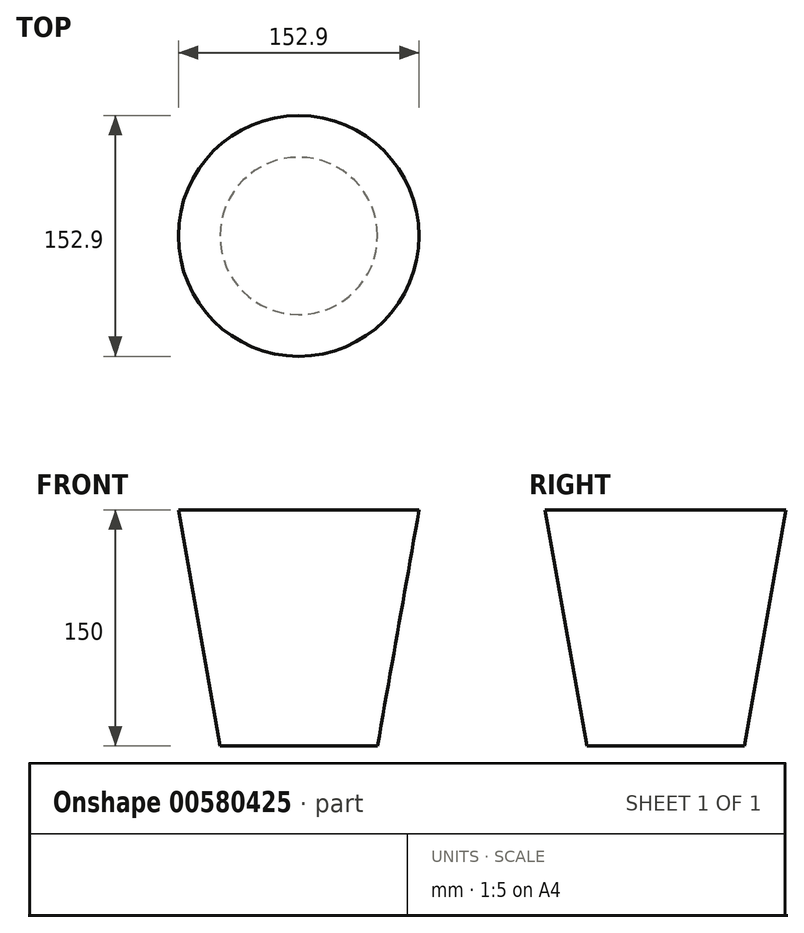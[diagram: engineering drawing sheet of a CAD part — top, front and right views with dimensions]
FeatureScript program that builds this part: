
annotation { "Feature Type Name" : "Feature", "Feature Type Description" : "" }
export const myFeature = defineFeature(function(context is Context, id is Id, definition is map)
    precondition{}
    {
        {
            var Q0;
            Q0=qCreatedBy(makeId("Top.planeOp"),FACE);
            var sketch = newSketch(context, id + "F0", { "sketchPlane" : qUnion([Q0])});
            skCircle(sketch, "E0", {"center": v(0, 0) * mm, "radius": 50 * mm});
            skSolve(sketch);
        }
        {
            var Q0;
            Q0=makeQuery(id+"F0.imprint","IMPRINT",FACE,{"disambiguationData":[TD([[makeQuery(id+"F0.imprint","IMPRINT",EDGE,{"derivedFrom":sQuery(id+"F0.wireOp",EDGE,"E0")}),1.0]])]});
            extrude(context, id + "F1", {"entities" : qUnion([Q0]), "depth" : 150 * mm, "offsetDistance" : 25 * mm, "hasDraft" : true, "draftAngle" : 10 * degree});
        }
    });
